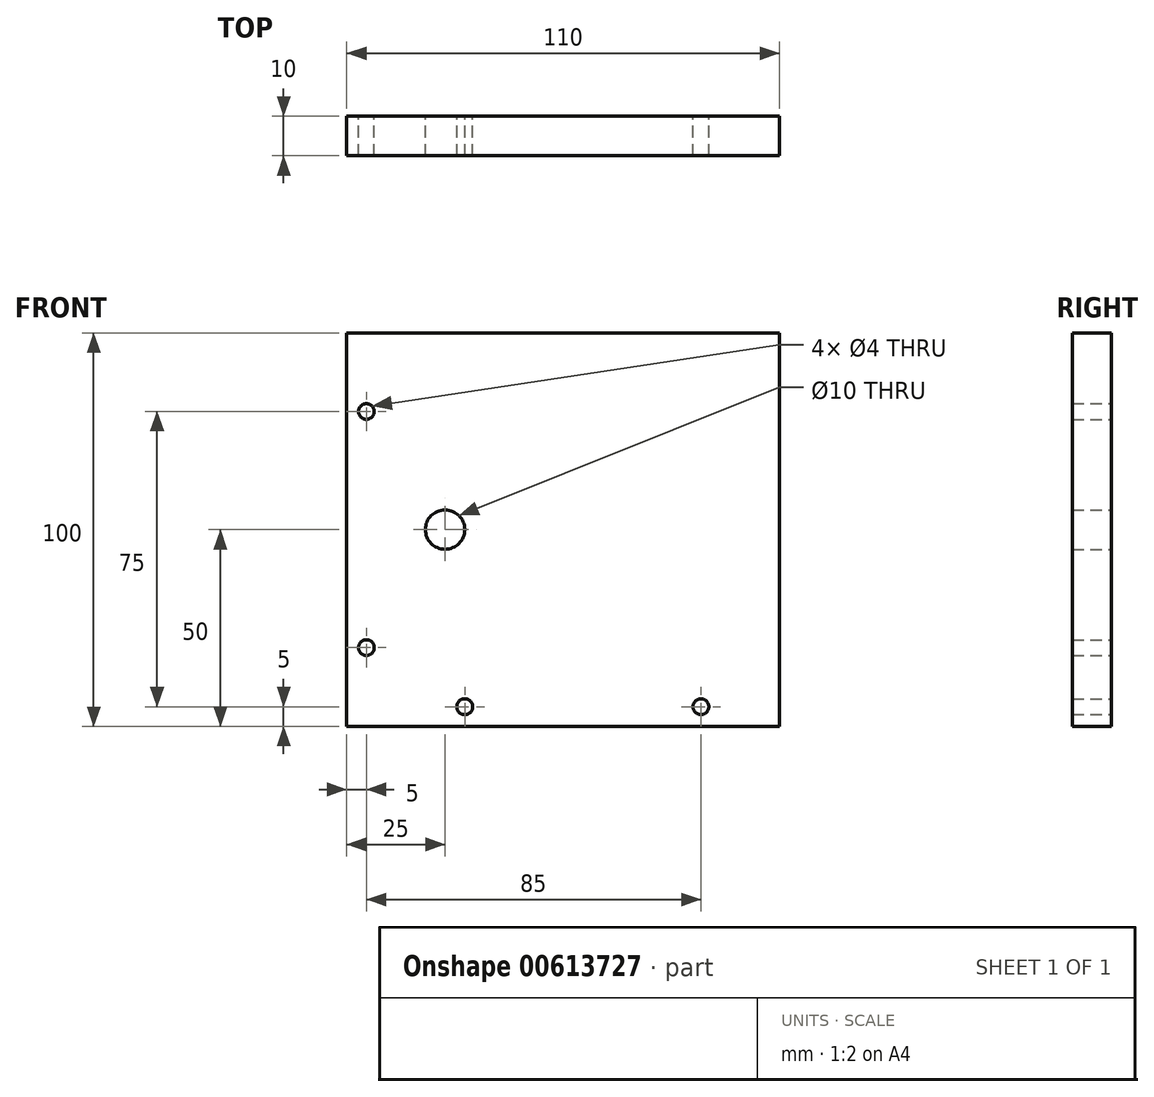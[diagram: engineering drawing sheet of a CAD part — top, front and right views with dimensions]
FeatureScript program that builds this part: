
annotation { "Feature Type Name" : "Feature", "Feature Type Description" : "" }
export const myFeature = defineFeature(function(context is Context, id is Id, definition is map)
    precondition{}
    {
        {
            var Q0;
            Q0=qCreatedBy(makeId("Front.planeOp"),FACE);
            var sketch = newSketch(context, id + "F0", { "sketchPlane" : qUnion([Q0])});
            skLineSegment(sketch, "E0.bottom", {"start": v(55, 50) * mm, "end": v(-55, 50) * mm});
            skLineSegment(sketch, "E0.top", {"start": v(55, -50) * mm, "end": v(-55, -50) * mm});
            skLineSegment(sketch, "E0.left", {"start": v(55, 50) * mm, "end": v(55, -50) * mm});
            skLineSegment(sketch, "E0.right", {"start": v(-55, 50) * mm, "end": v(-55, -50) * mm});
            skPoint(sketch, "E0.middle", {"position": v(0, 0) * mm});
            skCircle(sketch, "E1", {"center": v(-25, -45) * mm, "radius": 2 * mm});
            skCircle(sketch, "E2", {"center": v(35, -45) * mm, "radius": 2 * mm});
            skCircle(sketch, "E3", {"center": v(-50, 30) * mm, "radius": 2 * mm});
            skCircle(sketch, "E4", {"center": v(-50, -30) * mm, "radius": 2 * mm});
            skCircle(sketch, "E5", {"center": v(-30, 0) * mm, "radius": 5 * mm});
            skSolve(sketch);
        }
        {
            var Q0;
            Q0=makeQuery(id+"F0.imprint","IMPRINT",FACE,{"disambiguationData":[TD([[makeQuery(id+"F0.imprint","IMPRINT",EDGE,{"derivedFrom":sQuery(id+"F0.wireOp",EDGE,"E0.bottom")}),1.0]])]});
            extrude(context, id + "F1", {"entities" : qUnion([Q0]), "depth" : 10 * mm, "offsetDistance" : 25 * mm});
        }
    });
